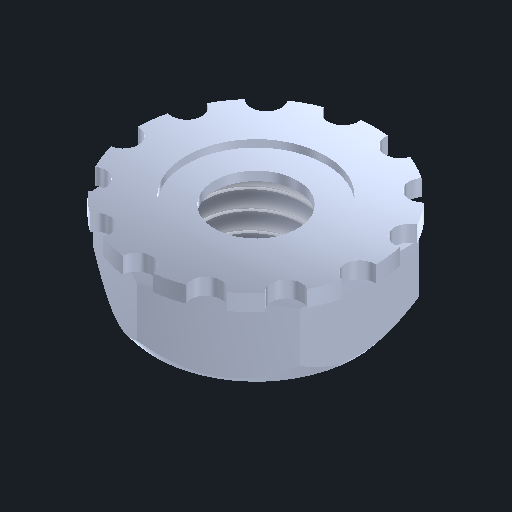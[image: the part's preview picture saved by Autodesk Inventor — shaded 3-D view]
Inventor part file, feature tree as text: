
AUTODESK INVENTOR PART (.ipt)
format: ipt  version: 2024 (Build 280153000, 153)  size: 305,152 bytes
history: native  units: in
note: dims shown in document units (in); Inventor stores cm internally (conversion verified against a paired STEP export)
features: other x2, imported_body x2, thread x1, extrude x1, projected_geometry x1
ambient origin geometry x8: Origin, YZ Plane, XZ Plane, XY Plane, X Axis, Y Axis, Z Axis, Center Point
bodies: Body1 (feature_tree), Body2 (feature_tree)
feature tree (7):
  parser-record x1  (decoder bookkeeping rows leaked as tree rows — omitted from the tree; the rows remain in map.json)
  imported_body  "Base1"
  imported_body  "Base2"
  thread  "Thread1"  [1 undecoded]
  extrude  "Extrusion1"  Depth=0.007in TaperAngle=0.0deg
  other  "NONE_1"
  projected_geometry  "Projected Loop1"
note: 1 required parameter value undecoded (feature->parameter linkage not recoverable at this tier; creation-order binding heuristic only, values carry confidence <= 0.55)
